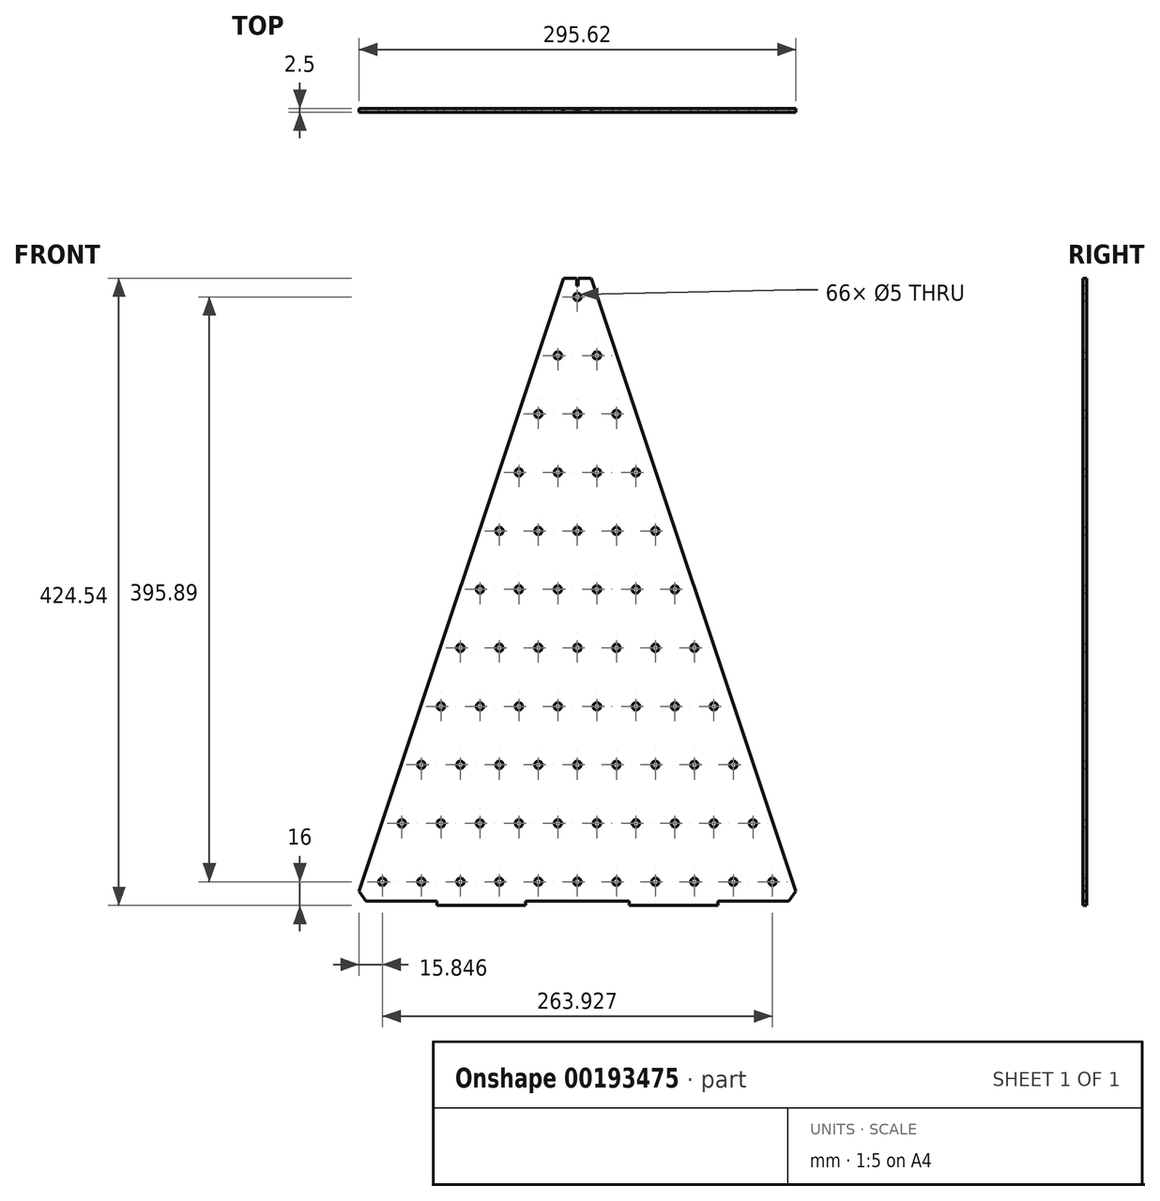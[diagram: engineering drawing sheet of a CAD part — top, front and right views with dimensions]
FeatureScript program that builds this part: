
annotation { "Feature Type Name" : "Feature", "Feature Type Description" : "" }
export const myFeature = defineFeature(function(context is Context, id is Id, definition is map)
    precondition{}
    {
        {
            var Q0;
            Q0=qCreatedBy(makeId("Front.planeOp"),FACE);
            var sketch = newSketch(context, id + "F0", { "sketchPlane" : qUnion([Q0])});
            skLineSegment(sketch, "E0", {"start": v(0, 450) * mm, "end": v(-150, 0) * mm});
            skLineSegment(sketch, "E1", {"start": v(-150, 0) * mm, "end": v(150, 0) * mm});
            skLineSegment(sketch, "E2", {"start": v(150, 0) * mm, "end": v(0, 450) * mm});
            skSolve(sketch);
        }
        {
            var Q0;
            Q0=makeQuery(id+"F0.imprint","IMPRINT",FACE,{"disambiguationData":[TD([[makeQuery(id+"F0.imprint","IMPRINT",EDGE,{"derivedFrom":sQuery(id+"F0.wireOp",EDGE,"E0")}),1.0]])]});
            extrude(context, id + "F1", {"entities" : qUnion([Q0]), "depth" : 2.5 * mm});
        }
        {
            var Q0;
            Q0=makeQuery(id+"F1.opExtrude","SWEPT_EDGE",EDGE,{"disambiguationData":[OSD([sQuery(id+"F0.wireOp",EDGE,"E1"),sQuery(id+"F0.wireOp",EDGE,"E2")])]});
            var Q1;
            Q1=makeQuery(id+"F1.opExtrude","SWEPT_EDGE",EDGE,{"disambiguationData":[OSD([sQuery(id+"F0.wireOp",EDGE,"E0"),sQuery(id+"F0.wireOp",EDGE,"E1")])]});
            chamfer(context, id + "F10", {"entities" : qUnion([Q0, Q1]), "width" : 5 * mm, "tangentPropagation" : true});
        }
        {
            var Q0;
            Q0=qCreatedBy(makeId("Front.planeOp"),FACE);
            var sketch = newSketch(context, id + "F2", { "sketchPlane" : qUnion([Q0])});
            skLineSegment(sketch, "E3.bottom", {"start": v(-35, 0) * mm, "end": v(-95, 0) * mm});
            skLineSegment(sketch, "E3.top", {"start": v(-35, -3) * mm, "end": v(-95, -3) * mm});
            skLineSegment(sketch, "E3.left", {"start": v(-35, 0) * mm, "end": v(-35, -3) * mm});
            skLineSegment(sketch, "E3.right", {"start": v(-95, 0) * mm, "end": v(-95, -3) * mm});
            skLineSegment(sketch, "E4.bottom", {"start": v(35, 0) * mm, "end": v(95, 0) * mm});
            skLineSegment(sketch, "E4.top", {"start": v(35, -3) * mm, "end": v(95, -3) * mm});
            skLineSegment(sketch, "E4.left", {"start": v(35, 0) * mm, "end": v(35, -3) * mm});
            skLineSegment(sketch, "E4.right", {"start": v(95, 0) * mm, "end": v(95, -3) * mm});
            skLineSegment(sketch, "E5", {"start": v(0, 0) * mm, "end": v(0, -3) * mm, "construction": true});
            skSolve(sketch);
        }
        {
            var Q0;
            Q0=makeQuery(id+"F2.imprint","IMPRINT",FACE,{"disambiguationData":[TD([[makeQuery(id+"F2.imprint","IMPRINT",EDGE,{"derivedFrom":sQuery(id+"F2.wireOp",EDGE,"E3.bottom")}),1.0]])]});
            var Q1;
            Q1=makeQuery(id+"F2.imprint","IMPRINT",FACE,{"disambiguationData":[TD([[makeQuery(id+"F2.imprint","IMPRINT",EDGE,{"derivedFrom":sQuery(id+"F2.wireOp",EDGE,"E4.bottom")}),-1.0]])]});
            extrude(context, id + "F3", {"entities" : qUnion([Q0, Q1]), "operationType" : NewBodyOperationType.ADD, "depth" : 2.5 * mm});
        }
        {
            var Q0;
            Q0=makeQuery(id+"F1.opExtrude","SWEPT_EDGE",EDGE,{"disambiguationData":[OSD([sQuery(id+"F0.wireOp",EDGE,"E0"),sQuery(id+"F0.wireOp",EDGE,"E2")])]});
            chamfer(context, id + "F4", {"entities" : qUnion([Q0]), "width" : 10 * mm, "tangentPropagation" : true});
        }
        {
            var Q0;
            Q0=makeQuery(id+"F4.opChamfer","BLEND_FACE",FACE,{"disambiguationData":[OSD([sQuery(id+"F0.wireOp",EDGE,"E0"),sQuery(id+"F0.wireOp",EDGE,"E2")])]});
            var sketch = newSketch(context, id + "F5", { "sketchPlane" : qUnion([Q0])});
            skLineSegment(sketch, "E6.bottom", {"start": v(0.5, 0) * mm, "end": v(-0.5, 0) * mm});
            skLineSegment(sketch, "E6.top", {"start": v(0.5, -2.5) * mm, "end": v(-0.5, -2.5) * mm});
            skLineSegment(sketch, "E6.left", {"start": v(0.5, 0) * mm, "end": v(0.5, -2.5) * mm});
            skLineSegment(sketch, "E6.right", {"start": v(-0.5, 0) * mm, "end": v(-0.5, -2.5) * mm});
            skLineSegment(sketch, "E7", {"start": v(0, 0) * mm, "end": v(0, -2.5) * mm, "construction": true});
            skSolve(sketch);
        }
        {
            var Q0;
            Q0 = qSketchRegion(id + "F5", true);
            extrude(context, id + "F6", {"entities" : qUnion([Q0]), "operationType" : NewBodyOperationType.REMOVE, "oppositeDirection" : true, "depth" : 5 * mm});
        }
        {
            var Q0;
            Q0=qCreatedBy(makeId("Front.planeOp"),FACE);
            var sketch = newSketch(context, id + "F7", { "sketchPlane" : qUnion([Q0])});
            skLineSegment(sketch, "E8", {"start": v(-135.3, 3) * mm, "end": v(135.3, 3) * mm, "construction": true});
            skLineSegment(sketch, "E9", {"start": v(135.3, 3) * mm, "end": v(0, 408.9) * mm, "construction": true});
            skLineSegment(sketch, "E10", {"start": v(0, 408.9) * mm, "end": v(-135.3, 3) * mm, "construction": true});
            skLineSegment(sketch, "E11", {"start": v(0, 0) * mm, "end": v(0, 408.9) * mm, "construction": true});
            skLineSegment(sketch, "E12", {"start": v(-131.96, 13) * mm, "end": v(-105.57, 13) * mm, "construction": true});
            skLineSegment(sketch, "E13.1.0.0", {"start": v(-105.57, 13) * mm, "end": v(-79.18, 13) * mm, "construction": true});
            skLineSegment(sketch, "E13.2.0.0", {"start": v(-79.18, 13) * mm, "end": v(-52.79, 13) * mm, "construction": true});
            skLineSegment(sketch, "E13.3.0.0", {"start": v(-52.79, 13) * mm, "end": v(-26.4, 13) * mm, "construction": true});
            skLineSegment(sketch, "E13.4.0.0", {"start": v(-26.4, 13) * mm, "end": v(0, 13) * mm, "construction": true});
            skLineSegment(sketch, "E13.5.0.0", {"start": v(0, 13) * mm, "end": v(26.4, 13) * mm, "construction": true});
            skLineSegment(sketch, "E13.6.0.0", {"start": v(26.4, 13) * mm, "end": v(52.79, 13) * mm, "construction": true});
            skLineSegment(sketch, "E13.7.0.0", {"start": v(52.79, 13) * mm, "end": v(79.18, 13) * mm, "construction": true});
            skLineSegment(sketch, "E13.8.0.0", {"start": v(79.18, 13) * mm, "end": v(105.57, 13) * mm, "construction": true});
            skLineSegment(sketch, "E13.9.0.0", {"start": v(105.57, 13) * mm, "end": v(131.96, 13) * mm, "construction": true});
            skPoint(sketch, "E14", {"position": v(-131.96, 13) * mm});
            skPoint(sketch, "E15", {"position": v(-105.57, 13) * mm});
            skPoint(sketch, "E16", {"position": v(-79.18, 13) * mm});
            skPoint(sketch, "E17", {"position": v(-52.79, 13) * mm});
            skPoint(sketch, "E18", {"position": v(-26.4, 13) * mm});
            skPoint(sketch, "E19", {"position": v(0, 13) * mm});
            skPoint(sketch, "E20", {"position": v(26.4, 13) * mm});
            skPoint(sketch, "E21", {"position": v(52.79, 13) * mm});
            skPoint(sketch, "E22", {"position": v(79.18, 13) * mm});
            skPoint(sketch, "E23", {"position": v(105.57, 13) * mm});
            skPoint(sketch, "E24", {"position": v(131.96, 13) * mm});
            skLineSegment(sketch, "E25.0.1.0", {"start": v(92.37, 52.59) * mm, "end": v(118.77, 52.59) * mm, "construction": true});
            skLineSegment(sketch, "E25.0.1.1", {"start": v(39.59, 52.59) * mm, "end": v(65.98, 52.59) * mm, "construction": true});
            skPoint(sketch, "E25.0.1.2", {"position": v(-118.77, 52.59) * mm});
            skPoint(sketch, "E25.0.1.3", {"position": v(65.98, 52.59) * mm});
            skPoint(sketch, "E25.0.1.4", {"position": v(92.37, 52.59) * mm});
            skLineSegment(sketch, "E25.0.1.5", {"start": v(-13.2, 52.59) * mm, "end": v(13.2, 52.59) * mm, "construction": true});
            skPoint(sketch, "E25.0.1.6", {"position": v(-92.37, 52.59) * mm});
            skLineSegment(sketch, "E25.0.1.7", {"start": v(65.98, 52.59) * mm, "end": v(92.37, 52.59) * mm, "construction": true});
            skLineSegment(sketch, "E25.0.1.8", {"start": v(13.2, 52.59) * mm, "end": v(39.59, 52.59) * mm, "construction": true});
            skLineSegment(sketch, "E25.0.1.9", {"start": v(-39.59, 52.59) * mm, "end": v(-13.2, 52.59) * mm, "construction": true});
            skLineSegment(sketch, "E25.0.1.10", {"start": v(-65.98, 52.59) * mm, "end": v(-39.59, 52.59) * mm, "construction": true});
            skLineSegment(sketch, "E25.0.1.11", {"start": v(-92.37, 52.59) * mm, "end": v(-65.98, 52.59) * mm, "construction": true});
            skPoint(sketch, "E25.0.1.12", {"position": v(-65.98, 52.59) * mm});
            skLineSegment(sketch, "E25.0.1.13", {"start": v(-118.77, 52.59) * mm, "end": v(-92.37, 52.59) * mm, "construction": true});
            skPoint(sketch, "E25.0.1.14", {"position": v(-39.59, 52.59) * mm});
            skPoint(sketch, "E25.0.1.15", {"position": v(-13.2, 52.59) * mm});
            skPoint(sketch, "E25.0.1.16", {"position": v(118.77, 52.59) * mm});
            skLineSegment(sketch, "E25.0.1.17", {"start": v(118.77, 52.59) * mm, "end": v(145.16, 52.59) * mm, "construction": true});
            skPoint(sketch, "E25.0.1.18", {"position": v(39.59, 52.59) * mm});
            skPoint(sketch, "E25.0.1.19", {"position": v(145.16, 52.59) * mm});
            skPoint(sketch, "E25.0.1.20", {"position": v(13.2, 52.59) * mm});
            skLineSegment(sketch, "E25.0.1.21", {"start": v(-118.77, 52.59) * mm, "end": v(-92.37, 52.59) * mm, "construction": true});
            skLineSegment(sketch, "E25.0.2.0", {"start": v(105.57, 92.18) * mm, "end": v(131.96, 92.18) * mm, "construction": true});
            skLineSegment(sketch, "E25.0.2.1", {"start": v(52.79, 92.18) * mm, "end": v(79.18, 92.18) * mm, "construction": true});
            skPoint(sketch, "E25.0.2.2", {"position": v(-105.57, 92.18) * mm});
            skPoint(sketch, "E25.0.2.3", {"position": v(79.18, 92.18) * mm});
            skPoint(sketch, "E25.0.2.4", {"position": v(105.57, 92.18) * mm});
            skLineSegment(sketch, "E25.0.2.5", {"start": v(0, 92.18) * mm, "end": v(26.4, 92.18) * mm, "construction": true});
            skPoint(sketch, "E25.0.2.6", {"position": v(-79.18, 92.18) * mm});
            skLineSegment(sketch, "E25.0.2.7", {"start": v(79.18, 92.18) * mm, "end": v(105.57, 92.18) * mm, "construction": true});
            skLineSegment(sketch, "E25.0.2.8", {"start": v(26.4, 92.18) * mm, "end": v(52.79, 92.18) * mm, "construction": true});
            skLineSegment(sketch, "E25.0.2.9", {"start": v(-26.4, 92.18) * mm, "end": v(0, 92.18) * mm, "construction": true});
            skLineSegment(sketch, "E25.0.2.10", {"start": v(-52.79, 92.18) * mm, "end": v(-26.4, 92.18) * mm, "construction": true});
            skLineSegment(sketch, "E25.0.2.11", {"start": v(-79.18, 92.18) * mm, "end": v(-52.79, 92.18) * mm, "construction": true});
            skPoint(sketch, "E25.0.2.12", {"position": v(-52.79, 92.18) * mm});
            skLineSegment(sketch, "E25.0.2.13", {"start": v(-105.57, 92.18) * mm, "end": v(-79.18, 92.18) * mm, "construction": true});
            skPoint(sketch, "E25.0.2.14", {"position": v(-26.4, 92.18) * mm});
            skPoint(sketch, "E25.0.2.15", {"position": v(0, 92.18) * mm});
            skPoint(sketch, "E25.0.2.16", {"position": v(131.96, 92.18) * mm});
            skLineSegment(sketch, "E25.0.2.17", {"start": v(131.96, 92.18) * mm, "end": v(158.36, 92.18) * mm, "construction": true});
            skPoint(sketch, "E25.0.2.18", {"position": v(52.79, 92.18) * mm});
            skPoint(sketch, "E25.0.2.19", {"position": v(158.36, 92.18) * mm});
            skPoint(sketch, "E25.0.2.20", {"position": v(26.4, 92.18) * mm});
            skLineSegment(sketch, "E25.0.2.21", {"start": v(-105.57, 92.18) * mm, "end": v(-79.18, 92.18) * mm, "construction": true});
            skLineSegment(sketch, "E25.0.3.0", {"start": v(118.77, 131.77) * mm, "end": v(145.16, 131.77) * mm, "construction": true});
            skLineSegment(sketch, "E25.0.3.1", {"start": v(65.98, 131.77) * mm, "end": v(92.37, 131.77) * mm, "construction": true});
            skPoint(sketch, "E25.0.3.2", {"position": v(-92.37, 131.77) * mm});
            skPoint(sketch, "E25.0.3.3", {"position": v(92.37, 131.77) * mm});
            skPoint(sketch, "E25.0.3.4", {"position": v(118.77, 131.77) * mm});
            skLineSegment(sketch, "E25.0.3.5", {"start": v(13.2, 131.77) * mm, "end": v(39.59, 131.77) * mm, "construction": true});
            skPoint(sketch, "E25.0.3.6", {"position": v(-65.98, 131.77) * mm});
            skLineSegment(sketch, "E25.0.3.7", {"start": v(92.37, 131.77) * mm, "end": v(118.77, 131.77) * mm, "construction": true});
            skLineSegment(sketch, "E25.0.3.8", {"start": v(39.59, 131.77) * mm, "end": v(65.98, 131.77) * mm, "construction": true});
            skLineSegment(sketch, "E25.0.3.9", {"start": v(-13.2, 131.77) * mm, "end": v(13.2, 131.77) * mm, "construction": true});
            skLineSegment(sketch, "E25.0.3.10", {"start": v(-39.59, 131.77) * mm, "end": v(-13.2, 131.77) * mm, "construction": true});
            skLineSegment(sketch, "E25.0.3.11", {"start": v(-65.98, 131.77) * mm, "end": v(-39.59, 131.77) * mm, "construction": true});
            skPoint(sketch, "E25.0.3.12", {"position": v(-39.59, 131.77) * mm});
            skLineSegment(sketch, "E25.0.3.13", {"start": v(-92.37, 131.77) * mm, "end": v(-65.98, 131.77) * mm, "construction": true});
            skPoint(sketch, "E25.0.3.14", {"position": v(-13.2, 131.77) * mm});
            skPoint(sketch, "E25.0.3.15", {"position": v(13.2, 131.77) * mm});
            skPoint(sketch, "E25.0.3.16", {"position": v(145.16, 131.77) * mm});
            skLineSegment(sketch, "E25.0.3.17", {"start": v(145.16, 131.77) * mm, "end": v(171.55, 131.77) * mm, "construction": true});
            skPoint(sketch, "E25.0.3.18", {"position": v(65.98, 131.77) * mm});
            skPoint(sketch, "E25.0.3.19", {"position": v(171.55, 131.77) * mm});
            skPoint(sketch, "E25.0.3.20", {"position": v(39.59, 131.77) * mm});
            skLineSegment(sketch, "E25.0.3.21", {"start": v(-92.37, 131.77) * mm, "end": v(-65.98, 131.77) * mm, "construction": true});
            skLineSegment(sketch, "E25.0.4.0", {"start": v(131.96, 171.36) * mm, "end": v(158.36, 171.36) * mm, "construction": true});
            skLineSegment(sketch, "E25.0.4.1", {"start": v(79.18, 171.36) * mm, "end": v(105.57, 171.36) * mm, "construction": true});
            skPoint(sketch, "E25.0.4.2", {"position": v(-79.18, 171.36) * mm});
            skPoint(sketch, "E25.0.4.3", {"position": v(105.57, 171.36) * mm});
            skPoint(sketch, "E25.0.4.4", {"position": v(131.96, 171.36) * mm});
            skLineSegment(sketch, "E25.0.4.5", {"start": v(26.4, 171.36) * mm, "end": v(52.79, 171.36) * mm, "construction": true});
            skPoint(sketch, "E25.0.4.6", {"position": v(-52.79, 171.36) * mm});
            skLineSegment(sketch, "E25.0.4.7", {"start": v(105.57, 171.36) * mm, "end": v(131.96, 171.36) * mm, "construction": true});
            skLineSegment(sketch, "E25.0.4.8", {"start": v(52.79, 171.36) * mm, "end": v(79.18, 171.36) * mm, "construction": true});
            skLineSegment(sketch, "E25.0.4.9", {"start": v(0, 171.36) * mm, "end": v(26.4, 171.36) * mm, "construction": true});
            skLineSegment(sketch, "E25.0.4.10", {"start": v(-26.4, 171.36) * mm, "end": v(0, 171.36) * mm, "construction": true});
            skLineSegment(sketch, "E25.0.4.11", {"start": v(-52.79, 171.36) * mm, "end": v(-26.4, 171.36) * mm, "construction": true});
            skPoint(sketch, "E25.0.4.12", {"position": v(-26.4, 171.36) * mm});
            skLineSegment(sketch, "E25.0.4.13", {"start": v(-79.18, 171.36) * mm, "end": v(-52.79, 171.36) * mm, "construction": true});
            skPoint(sketch, "E25.0.4.14", {"position": v(0, 171.36) * mm});
            skPoint(sketch, "E25.0.4.15", {"position": v(26.4, 171.36) * mm});
            skPoint(sketch, "E25.0.4.16", {"position": v(158.36, 171.36) * mm});
            skLineSegment(sketch, "E25.0.4.17", {"start": v(158.36, 171.36) * mm, "end": v(184.75, 171.36) * mm, "construction": true});
            skPoint(sketch, "E25.0.4.18", {"position": v(79.18, 171.36) * mm});
            skPoint(sketch, "E25.0.4.19", {"position": v(184.75, 171.36) * mm});
            skPoint(sketch, "E25.0.4.20", {"position": v(52.79, 171.36) * mm});
            skLineSegment(sketch, "E25.0.4.21", {"start": v(-79.18, 171.36) * mm, "end": v(-52.79, 171.36) * mm, "construction": true});
            skLineSegment(sketch, "E25.0.5.0", {"start": v(145.16, 210.95) * mm, "end": v(171.55, 210.95) * mm, "construction": true});
            skLineSegment(sketch, "E25.0.5.1", {"start": v(92.37, 210.95) * mm, "end": v(118.77, 210.95) * mm, "construction": true});
            skPoint(sketch, "E25.0.5.2", {"position": v(-65.98, 210.95) * mm});
            skPoint(sketch, "E25.0.5.3", {"position": v(118.77, 210.95) * mm});
            skPoint(sketch, "E25.0.5.4", {"position": v(145.16, 210.95) * mm});
            skLineSegment(sketch, "E25.0.5.5", {"start": v(39.59, 210.95) * mm, "end": v(65.98, 210.95) * mm, "construction": true});
            skPoint(sketch, "E25.0.5.6", {"position": v(-39.59, 210.95) * mm});
            skLineSegment(sketch, "E25.0.5.7", {"start": v(118.77, 210.95) * mm, "end": v(145.16, 210.95) * mm, "construction": true});
            skLineSegment(sketch, "E25.0.5.8", {"start": v(65.98, 210.95) * mm, "end": v(92.37, 210.95) * mm, "construction": true});
            skLineSegment(sketch, "E25.0.5.9", {"start": v(13.2, 210.95) * mm, "end": v(39.59, 210.95) * mm, "construction": true});
            skLineSegment(sketch, "E25.0.5.10", {"start": v(-13.2, 210.95) * mm, "end": v(13.2, 210.95) * mm, "construction": true});
            skLineSegment(sketch, "E25.0.5.11", {"start": v(-39.59, 210.95) * mm, "end": v(-13.2, 210.95) * mm, "construction": true});
            skPoint(sketch, "E25.0.5.12", {"position": v(-13.2, 210.95) * mm});
            skLineSegment(sketch, "E25.0.5.13", {"start": v(-65.98, 210.95) * mm, "end": v(-39.59, 210.95) * mm, "construction": true});
            skPoint(sketch, "E25.0.5.14", {"position": v(13.2, 210.95) * mm});
            skPoint(sketch, "E25.0.5.15", {"position": v(39.59, 210.95) * mm});
            skPoint(sketch, "E25.0.5.16", {"position": v(171.55, 210.95) * mm});
            skLineSegment(sketch, "E25.0.5.17", {"start": v(171.55, 210.95) * mm, "end": v(197.95, 210.95) * mm, "construction": true});
            skPoint(sketch, "E25.0.5.18", {"position": v(92.37, 210.95) * mm});
            skPoint(sketch, "E25.0.5.19", {"position": v(197.95, 210.95) * mm});
            skPoint(sketch, "E25.0.5.20", {"position": v(65.98, 210.95) * mm});
            skLineSegment(sketch, "E25.0.5.21", {"start": v(-65.98, 210.95) * mm, "end": v(-39.59, 210.95) * mm, "construction": true});
            skLineSegment(sketch, "E25.0.6.0", {"start": v(158.36, 250.53) * mm, "end": v(184.75, 250.53) * mm, "construction": true});
            skLineSegment(sketch, "E25.0.6.1", {"start": v(105.57, 250.53) * mm, "end": v(131.96, 250.53) * mm, "construction": true});
            skPoint(sketch, "E25.0.6.2", {"position": v(-52.79, 250.53) * mm});
            skPoint(sketch, "E25.0.6.3", {"position": v(131.96, 250.53) * mm});
            skPoint(sketch, "E25.0.6.4", {"position": v(158.36, 250.53) * mm});
            skLineSegment(sketch, "E25.0.6.5", {"start": v(52.79, 250.53) * mm, "end": v(79.18, 250.53) * mm, "construction": true});
            skPoint(sketch, "E25.0.6.6", {"position": v(-26.4, 250.53) * mm});
            skLineSegment(sketch, "E25.0.6.7", {"start": v(131.96, 250.53) * mm, "end": v(158.36, 250.53) * mm, "construction": true});
            skLineSegment(sketch, "E25.0.6.8", {"start": v(79.18, 250.53) * mm, "end": v(105.57, 250.53) * mm, "construction": true});
            skLineSegment(sketch, "E25.0.6.9", {"start": v(26.4, 250.53) * mm, "end": v(52.79, 250.53) * mm, "construction": true});
            skLineSegment(sketch, "E25.0.6.10", {"start": v(0, 250.53) * mm, "end": v(26.4, 250.53) * mm, "construction": true});
            skLineSegment(sketch, "E25.0.6.11", {"start": v(-26.4, 250.53) * mm, "end": v(0, 250.53) * mm, "construction": true});
            skPoint(sketch, "E25.0.6.12", {"position": v(0, 250.53) * mm});
            skLineSegment(sketch, "E25.0.6.13", {"start": v(-52.79, 250.53) * mm, "end": v(-26.4, 250.53) * mm, "construction": true});
            skPoint(sketch, "E25.0.6.14", {"position": v(26.4, 250.53) * mm});
            skPoint(sketch, "E25.0.6.15", {"position": v(52.79, 250.53) * mm});
            skPoint(sketch, "E25.0.6.16", {"position": v(184.75, 250.53) * mm});
            skLineSegment(sketch, "E25.0.6.17", {"start": v(184.75, 250.53) * mm, "end": v(211.14, 250.53) * mm, "construction": true});
            skPoint(sketch, "E25.0.6.18", {"position": v(105.57, 250.53) * mm});
            skPoint(sketch, "E25.0.6.19", {"position": v(211.14, 250.53) * mm});
            skPoint(sketch, "E25.0.6.20", {"position": v(79.18, 250.53) * mm});
            skLineSegment(sketch, "E25.0.6.21", {"start": v(-52.79, 250.53) * mm, "end": v(-26.4, 250.53) * mm, "construction": true});
            skLineSegment(sketch, "E25.0.7.0", {"start": v(171.55, 290.12) * mm, "end": v(197.95, 290.12) * mm, "construction": true});
            skLineSegment(sketch, "E25.0.7.1", {"start": v(118.77, 290.12) * mm, "end": v(145.16, 290.12) * mm, "construction": true});
            skPoint(sketch, "E25.0.7.2", {"position": v(-39.59, 290.12) * mm});
            skPoint(sketch, "E25.0.7.3", {"position": v(145.16, 290.12) * mm});
            skPoint(sketch, "E25.0.7.4", {"position": v(171.55, 290.12) * mm});
            skLineSegment(sketch, "E25.0.7.5", {"start": v(65.98, 290.12) * mm, "end": v(92.37, 290.12) * mm, "construction": true});
            skPoint(sketch, "E25.0.7.6", {"position": v(-13.2, 290.12) * mm});
            skLineSegment(sketch, "E25.0.7.7", {"start": v(145.16, 290.12) * mm, "end": v(171.55, 290.12) * mm, "construction": true});
            skLineSegment(sketch, "E25.0.7.8", {"start": v(92.37, 290.12) * mm, "end": v(118.77, 290.12) * mm, "construction": true});
            skLineSegment(sketch, "E25.0.7.9", {"start": v(39.59, 290.12) * mm, "end": v(65.98, 290.12) * mm, "construction": true});
            skLineSegment(sketch, "E25.0.7.10", {"start": v(13.2, 290.12) * mm, "end": v(39.59, 290.12) * mm, "construction": true});
            skLineSegment(sketch, "E25.0.7.11", {"start": v(-13.2, 290.12) * mm, "end": v(13.2, 290.12) * mm, "construction": true});
            skPoint(sketch, "E25.0.7.12", {"position": v(13.2, 290.12) * mm});
            skLineSegment(sketch, "E25.0.7.13", {"start": v(-39.59, 290.12) * mm, "end": v(-13.2, 290.12) * mm, "construction": true});
            skPoint(sketch, "E25.0.7.14", {"position": v(39.59, 290.12) * mm});
            skPoint(sketch, "E25.0.7.15", {"position": v(65.98, 290.12) * mm});
            skPoint(sketch, "E25.0.7.16", {"position": v(197.95, 290.12) * mm});
            skLineSegment(sketch, "E25.0.7.17", {"start": v(197.95, 290.12) * mm, "end": v(224.34, 290.12) * mm, "construction": true});
            skPoint(sketch, "E25.0.7.18", {"position": v(118.77, 290.12) * mm});
            skPoint(sketch, "E25.0.7.19", {"position": v(224.34, 290.12) * mm});
            skPoint(sketch, "E25.0.7.20", {"position": v(92.37, 290.12) * mm});
            skLineSegment(sketch, "E25.0.7.21", {"start": v(-39.59, 290.12) * mm, "end": v(-13.2, 290.12) * mm, "construction": true});
            skLineSegment(sketch, "E25.0.8.0", {"start": v(184.75, 329.71) * mm, "end": v(211.14, 329.71) * mm, "construction": true});
            skLineSegment(sketch, "E25.0.8.1", {"start": v(131.96, 329.71) * mm, "end": v(158.36, 329.71) * mm, "construction": true});
            skPoint(sketch, "E25.0.8.2", {"position": v(-26.4, 329.71) * mm});
            skPoint(sketch, "E25.0.8.3", {"position": v(158.36, 329.71) * mm});
            skPoint(sketch, "E25.0.8.4", {"position": v(184.75, 329.71) * mm});
            skLineSegment(sketch, "E25.0.8.5", {"start": v(79.18, 329.71) * mm, "end": v(105.57, 329.71) * mm, "construction": true});
            skPoint(sketch, "E25.0.8.6", {"position": v(0, 329.71) * mm});
            skLineSegment(sketch, "E25.0.8.7", {"start": v(158.36, 329.71) * mm, "end": v(184.75, 329.71) * mm, "construction": true});
            skLineSegment(sketch, "E25.0.8.8", {"start": v(105.57, 329.71) * mm, "end": v(131.96, 329.71) * mm, "construction": true});
            skLineSegment(sketch, "E25.0.8.9", {"start": v(52.79, 329.71) * mm, "end": v(79.18, 329.71) * mm, "construction": true});
            skLineSegment(sketch, "E25.0.8.10", {"start": v(26.4, 329.71) * mm, "end": v(52.79, 329.71) * mm, "construction": true});
            skLineSegment(sketch, "E25.0.8.11", {"start": v(0, 329.71) * mm, "end": v(26.4, 329.71) * mm, "construction": true});
            skPoint(sketch, "E25.0.8.12", {"position": v(26.4, 329.71) * mm});
            skLineSegment(sketch, "E25.0.8.13", {"start": v(-26.4, 329.71) * mm, "end": v(0, 329.71) * mm, "construction": true});
            skPoint(sketch, "E25.0.8.14", {"position": v(52.79, 329.71) * mm});
            skPoint(sketch, "E25.0.8.15", {"position": v(79.18, 329.71) * mm});
            skPoint(sketch, "E25.0.8.16", {"position": v(211.14, 329.71) * mm});
            skLineSegment(sketch, "E25.0.8.17", {"start": v(211.14, 329.71) * mm, "end": v(237.53, 329.71) * mm, "construction": true});
            skPoint(sketch, "E25.0.8.18", {"position": v(131.96, 329.71) * mm});
            skPoint(sketch, "E25.0.8.19", {"position": v(237.53, 329.71) * mm});
            skPoint(sketch, "E25.0.8.20", {"position": v(105.57, 329.71) * mm});
            skLineSegment(sketch, "E25.0.8.21", {"start": v(-26.4, 329.71) * mm, "end": v(0, 329.71) * mm, "construction": true});
            skLineSegment(sketch, "E25.0.9.0", {"start": v(197.95, 369.3) * mm, "end": v(224.34, 369.3) * mm, "construction": true});
            skLineSegment(sketch, "E25.0.9.1", {"start": v(145.16, 369.3) * mm, "end": v(171.55, 369.3) * mm, "construction": true});
            skPoint(sketch, "E25.0.9.2", {"position": v(-13.2, 369.3) * mm});
            skPoint(sketch, "E25.0.9.3", {"position": v(171.55, 369.3) * mm});
            skPoint(sketch, "E25.0.9.4", {"position": v(197.95, 369.3) * mm});
            skLineSegment(sketch, "E25.0.9.5", {"start": v(92.37, 369.3) * mm, "end": v(118.77, 369.3) * mm, "construction": true});
            skPoint(sketch, "E25.0.9.6", {"position": v(13.2, 369.3) * mm});
            skLineSegment(sketch, "E25.0.9.7", {"start": v(171.55, 369.3) * mm, "end": v(197.95, 369.3) * mm, "construction": true});
            skLineSegment(sketch, "E25.0.9.8", {"start": v(118.77, 369.3) * mm, "end": v(145.16, 369.3) * mm, "construction": true});
            skLineSegment(sketch, "E25.0.9.9", {"start": v(65.98, 369.3) * mm, "end": v(92.37, 369.3) * mm, "construction": true});
            skLineSegment(sketch, "E25.0.9.10", {"start": v(39.59, 369.3) * mm, "end": v(65.98, 369.3) * mm, "construction": true});
            skLineSegment(sketch, "E25.0.9.11", {"start": v(13.2, 369.3) * mm, "end": v(39.59, 369.3) * mm, "construction": true});
            skPoint(sketch, "E25.0.9.12", {"position": v(39.59, 369.3) * mm});
            skLineSegment(sketch, "E25.0.9.13", {"start": v(-13.2, 369.3) * mm, "end": v(13.2, 369.3) * mm, "construction": true});
            skPoint(sketch, "E25.0.9.14", {"position": v(65.98, 369.3) * mm});
            skPoint(sketch, "E25.0.9.15", {"position": v(92.37, 369.3) * mm});
            skPoint(sketch, "E25.0.9.16", {"position": v(224.34, 369.3) * mm});
            skLineSegment(sketch, "E25.0.9.17", {"start": v(224.34, 369.3) * mm, "end": v(250.73, 369.3) * mm, "construction": true});
            skPoint(sketch, "E25.0.9.18", {"position": v(145.16, 369.3) * mm});
            skPoint(sketch, "E25.0.9.19", {"position": v(250.73, 369.3) * mm});
            skPoint(sketch, "E25.0.9.20", {"position": v(118.77, 369.3) * mm});
            skLineSegment(sketch, "E25.0.9.21", {"start": v(-13.2, 369.3) * mm, "end": v(13.2, 369.3) * mm, "construction": true});
            skLineSegment(sketch, "E25.0.10.0", {"start": v(211.14, 408.9) * mm, "end": v(237.53, 408.9) * mm, "construction": true});
            skLineSegment(sketch, "E25.0.10.1", {"start": v(158.36, 408.9) * mm, "end": v(184.75, 408.9) * mm, "construction": true});
            skPoint(sketch, "E25.0.10.2", {"position": v(0, 408.9) * mm});
            skPoint(sketch, "E25.0.10.3", {"position": v(184.75, 408.9) * mm});
            skPoint(sketch, "E25.0.10.4", {"position": v(211.14, 408.9) * mm});
            skLineSegment(sketch, "E25.0.10.5", {"start": v(105.57, 408.9) * mm, "end": v(131.96, 408.9) * mm, "construction": true});
            skPoint(sketch, "E25.0.10.6", {"position": v(26.4, 408.9) * mm});
            skLineSegment(sketch, "E25.0.10.7", {"start": v(184.75, 408.9) * mm, "end": v(211.14, 408.9) * mm, "construction": true});
            skLineSegment(sketch, "E25.0.10.8", {"start": v(131.96, 408.9) * mm, "end": v(158.36, 408.9) * mm, "construction": true});
            skLineSegment(sketch, "E25.0.10.9", {"start": v(79.18, 408.9) * mm, "end": v(105.57, 408.9) * mm, "construction": true});
            skLineSegment(sketch, "E25.0.10.10", {"start": v(52.79, 408.9) * mm, "end": v(79.18, 408.9) * mm, "construction": true});
            skLineSegment(sketch, "E25.0.10.11", {"start": v(26.4, 408.9) * mm, "end": v(52.79, 408.9) * mm, "construction": true});
            skPoint(sketch, "E25.0.10.12", {"position": v(52.79, 408.9) * mm});
            skLineSegment(sketch, "E25.0.10.13", {"start": v(0, 408.9) * mm, "end": v(26.4, 408.9) * mm, "construction": true});
            skPoint(sketch, "E25.0.10.14", {"position": v(79.18, 408.9) * mm});
            skPoint(sketch, "E25.0.10.15", {"position": v(105.57, 408.9) * mm});
            skPoint(sketch, "E25.0.10.16", {"position": v(237.53, 408.9) * mm});
            skLineSegment(sketch, "E25.0.10.17", {"start": v(237.53, 408.9) * mm, "end": v(263.93, 408.9) * mm, "construction": true});
            skPoint(sketch, "E25.0.10.18", {"position": v(158.36, 408.9) * mm});
            skPoint(sketch, "E25.0.10.19", {"position": v(263.93, 408.9) * mm});
            skPoint(sketch, "E25.0.10.20", {"position": v(131.96, 408.9) * mm});
            skLineSegment(sketch, "E25.0.10.21", {"start": v(0, 408.9) * mm, "end": v(26.4, 408.9) * mm, "construction": true});
            skLineSegment(sketch, "E25.direction1", {"start": v(-131.96, 13) * mm, "end": v(-106.96, 13) * mm, "construction": true});
            skLineSegment(sketch, "E25.direction2", {"start": v(-131.96, 13) * mm, "end": v(-118.77, 52.59) * mm, "construction": true});
            skSolve(sketch);
        }
        {
            var Q0;
            Q0=sQuery(id+"F7.wireOp",VERTEX,"E14");
            var Q1;
            Q1=sQuery(id+"F7.wireOp",VERTEX,"E15");
            var Q2;
            Q2=sQuery(id+"F7.wireOp",VERTEX,"E16");
            var Q3;
            Q3=sQuery(id+"F7.wireOp",VERTEX,"E17");
            var Q4;
            Q4=sQuery(id+"F7.wireOp",VERTEX,"E18");
            var Q5;
            Q5=sQuery(id+"F7.wireOp",VERTEX,"E19");
            var Q6;
            Q6=sQuery(id+"F7.wireOp",VERTEX,"E20");
            var Q7;
            Q7=sQuery(id+"F7.wireOp",VERTEX,"E21");
            var Q8;
            Q8=sQuery(id+"F7.wireOp",VERTEX,"E22");
            var Q9;
            Q9=sQuery(id+"F7.wireOp",VERTEX,"E23");
            var Q10;
            Q10=sQuery(id+"F7.wireOp",VERTEX,"E24");
            var Q11;
            Q11=sQuery(id+"F7.wireOp",VERTEX,"E25.0.1.16");
            var Q12;
            Q12=sQuery(id+"F7.wireOp",VERTEX,"E25.0.1.4");
            var Q13;
            Q13=sQuery(id+"F7.wireOp",VERTEX,"E25.0.2.12");
            var Q14;
            Q14=sQuery(id+"F7.wireOp",VERTEX,"E25.0.5.6");
            var Q15;
            Q15=sQuery(id+"F7.wireOp",VERTEX,"E25.0.1.18");
            var Q16;
            Q16=sQuery(id+"F7.wireOp",VERTEX,"E25.0.2.14");
            var Q17;
            Q17=sQuery(id+"F7.wireOp",VERTEX,"E25.0.1.2");
            var Q18;
            Q18=sQuery(id+"F7.wireOp",VERTEX,"E25.0.5.12");
            var Q19;
            Q19=sQuery(id+"F7.wireOp",VERTEX,"E25.0.3.20");
            var Q20;
            Q20=sQuery(id+"F7.wireOp",VERTEX,"E25.0.3.6");
            var Q21;
            Q21=sQuery(id+"F7.wireOp",VERTEX,"E25.0.2.15");
            var Q22;
            Q22=sQuery(id+"F7.wireOp",VERTEX,"E25.0.5.14");
            var Q23;
            Q23=sQuery(id+"F7.wireOp",VERTEX,"E25.0.4.2");
            var Q24;
            Q24=sQuery(id+"F7.wireOp",VERTEX,"E25.0.3.12");
            var Q25;
            Q25=sQuery(id+"F7.wireOp",VERTEX,"E25.0.1.20");
            var Q26;
            Q26=sQuery(id+"F7.wireOp",VERTEX,"E25.0.6.6");
            var Q27;
            Q27=sQuery(id+"F7.wireOp",VERTEX,"E25.0.7.2");
            var Q28;
            Q28=sQuery(id+"F7.wireOp",VERTEX,"E25.0.5.15");
            var Q29;
            Q29=sQuery(id+"F7.wireOp",VERTEX,"E25.0.4.6");
            var Q30;
            Q30=sQuery(id+"F7.wireOp",VERTEX,"E25.0.3.14");
            var Q31;
            Q31=sQuery(id+"F7.wireOp",VERTEX,"E25.0.2.2");
            var Q32;
            Q32=sQuery(id+"F7.wireOp",VERTEX,"E25.0.1.12");
            var Q33;
            Q33=sQuery(id+"F7.wireOp",VERTEX,"E25.0.6.12");
            var Q34;
            Q34=sQuery(id+"F7.wireOp",VERTEX,"E25.0.1.6");
            var Q35;
            Q35=sQuery(id+"F7.wireOp",VERTEX,"E25.0.5.2");
            var Q36;
            Q36=sQuery(id+"F7.wireOp",VERTEX,"E25.0.4.12");
            var Q37;
            Q37=sQuery(id+"F7.wireOp",VERTEX,"E25.0.3.15");
            var Q38;
            Q38=sQuery(id+"F7.wireOp",VERTEX,"E25.0.2.20");
            var Q39;
            Q39=sQuery(id+"F7.wireOp",VERTEX,"E25.0.1.14");
            var Q40;
            Q40=sQuery(id+"F7.wireOp",VERTEX,"E25.0.7.6");
            var Q41;
            Q41=sQuery(id+"F7.wireOp",VERTEX,"E25.0.6.14");
            var Q42;
            Q42=sQuery(id+"F7.wireOp",VERTEX,"E25.0.4.14");
            var Q43;
            Q43=sQuery(id+"F7.wireOp",VERTEX,"E25.0.3.2");
            var Q44;
            Q44=sQuery(id+"F7.wireOp",VERTEX,"E25.0.1.15");
            var Q45;
            Q45=sQuery(id+"F7.wireOp",VERTEX,"E25.0.7.12");
            var Q46;
            Q46=sQuery(id+"F7.wireOp",VERTEX,"E25.0.2.6");
            var Q47;
            Q47=sQuery(id+"F7.wireOp",VERTEX,"E25.0.4.15");
            var Q48;
            Q48=sQuery(id+"F7.wireOp",VERTEX,"E25.0.7.14");
            var Q49;
            Q49=sQuery(id+"F7.wireOp",VERTEX,"E25.0.6.2");
            var Q50;
            Q50=sQuery(id+"F7.wireOp",VERTEX,"E25.0.5.20");
            var Q51;
            Q51=sQuery(id+"F7.wireOp",VERTEX,"E25.0.6.15");
            var Q52;
            Q52=sQuery(id+"F7.wireOp",VERTEX,"E25.0.4.20");
            var Q53;
            Q53=sQuery(id+"F7.wireOp",VERTEX,"E25.0.4.18");
            var Q54;
            Q54=sQuery(id+"F7.wireOp",VERTEX,"E25.0.3.18");
            var Q55;
            Q55=sQuery(id+"F7.wireOp",VERTEX,"E25.0.2.18");
            var Q56;
            Q56=sQuery(id+"F7.wireOp",VERTEX,"E25.0.2.3");
            var Q57;
            Q57=sQuery(id+"F7.wireOp",VERTEX,"E25.0.3.3");
            var Q58;
            Q58=sQuery(id+"F7.wireOp",VERTEX,"E25.0.2.4");
            var Q59;
            Q59=sQuery(id+"F7.wireOp",VERTEX,"E25.0.1.3");
            var Q60;
            Q60=sQuery(id+"F7.wireOp",VERTEX,"E25.0.8.12");
            var Q61;
            Q61=sQuery(id+"F7.wireOp",VERTEX,"E25.0.9.6");
            var Q62;
            Q62=sQuery(id+"F7.wireOp",VERTEX,"E25.0.10.2");
            var Q63;
            Q63=sQuery(id+"F7.wireOp",VERTEX,"E25.0.9.2");
            var Q64;
            Q64=sQuery(id+"F7.wireOp",VERTEX,"E25.0.8.2");
            var Q65;
            Q65=sQuery(id+"F7.wireOp",VERTEX,"E25.0.8.6");
            var Q66;
            Q66=sQuery(id+"F7.wireOp",VERTEX,"E25.0.8.12");
            var Q67;
            Q67=sQuery(id+"F7.wireOp",VERTEX,"E25.0.4.18");
            var Q68;
            Q68=sQuery(id+"F7.wireOp",VERTEX,"E25.0.3.18");
            var Q69;
            Q69=sQuery(id+"F7.wireOp",VERTEX,"E25.0.2.18");
            var Q70;
            Q70=sQuery(id+"F7.wireOp",VERTEX,"E25.0.2.3");
            var Q71;
            Q71=sQuery(id+"F7.wireOp",VERTEX,"E25.0.3.3");
            var Q72;
            Q72=sQuery(id+"F7.wireOp",VERTEX,"E25.0.2.4");
            var Q73;
            Q73=sQuery(id+"F7.wireOp",VERTEX,"E25.0.3.3");
            var Q74;
            Q74=sQuery(id+"F7.wireOp",VERTEX,"E25.0.2.4");
            var Q75;
            Q75=makeQuery(id+"F1.opExtrude","SWEPT_BODY",BODY,{"disambiguationData":[OSD([sQuery(id+"F0.wireOp",EDGE,"E0"),sQuery(id+"F0.wireOp",EDGE,"E1"),sQuery(id+"F0.wireOp",EDGE,"E2")])]});
            hole(context, id + "F8", {"style" : HoleStyle.SIMPLE, "endStyle" : HoleEndStyle.THROUGH, "oppositeDirection" : true, "holeDiameter" : 5 * mm, "locations" : qUnion([Q0, Q1, Q2, Q3, Q4, Q5, Q6, Q7, Q8, Q9, Q10, Q11, Q12, Q13, Q14, Q15, Q16, Q17, Q18, Q19, Q20, Q21, Q22, Q23, Q24, Q25, Q26, Q27, Q28, Q29, Q30, Q31, Q32, Q33, Q34, Q35, Q36, Q37, Q38, Q39, Q40, Q41, Q42, Q43, Q44, Q45, Q46, Q47, Q48, Q49, Q50, Q51, Q52, Q53, Q54, Q55, Q56, Q57, Q58, Q59, Q60, Q61, Q62, Q63, Q64, Q65, Q66, Q67, Q68, Q69, Q70, Q71, Q72, Q73, Q74]), "scope" : qUnion([Q75]), "tappedDepth" : 12 * mm, "tapClearance" : 3});
        }
    });
